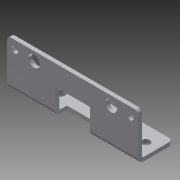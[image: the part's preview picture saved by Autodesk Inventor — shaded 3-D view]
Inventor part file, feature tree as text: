
AUTODESK INVENTOR PART (.ipt)
format: ipt  version: 2013 (Build 170138000, 138)  size: 263,680 bytes
history: native  units: in
note: dims shown in document units (in); Inventor stores cm internally (conversion verified against a paired STEP export)
features: other x7, sketch x6, sheet_metal_op x4, reference x3, chamfer x1, plane x1
ambient origin geometry x8: Origin, YZ Plane, XZ Plane, XY Plane, X Axis, Y Axis, Z Axis, Center Point
bodies: Solid1 (feature_tree)
feature tree (22):
  sheet_metal_op  "Face1"
  sheet_metal_op  "Flange1"
  chamfer  "Corner Round1"
  plane  "Work Plane1"
  sketch  "Sketch1"  dims[d0=4.25in]
  other  "Plate1"
  sketch  "Sketch2"  dims[d1=1.125in]
  other  "Plate2"
  sheet_metal_op  "Bend1"
  sheet_metal_op  "Corner1"
  sketch  "Sketch3"  dims[d3=0.125in]
  sketch  "Sketch4"  dims[d4=0.125in]
  sketch  "Sketch5"  dims[d5=0.0625in]
  reference  "Reference1"
  sketch  "Sketch6"  dims[d6=0.25in d7=0.125in d8=1.5in d9=90.0deg d10=0.05in d11=0.5in d12=0.125in d13=0.125in d18=1.125in d20=0.375in d21=0.0in d22=0.625in d23=0.26in d24=0.26in d25=2.0in d26=1.0in d27=0.125in d28=0.0in d29=0.125in d30=0.125in d31=0.0in d32=0.125in d33=0.0in d34=0.375in d35=0.375in d36=0.875in d37=0.875in d38=0.25in d39=0.25in d2=0.125in]
  reference  "Reference11"
  reference  "Reference12"
  other  "Cut1"
  other  "Cut2"
  other  "Cut3"
  other  "Cut4"
  other  "Definition1"
